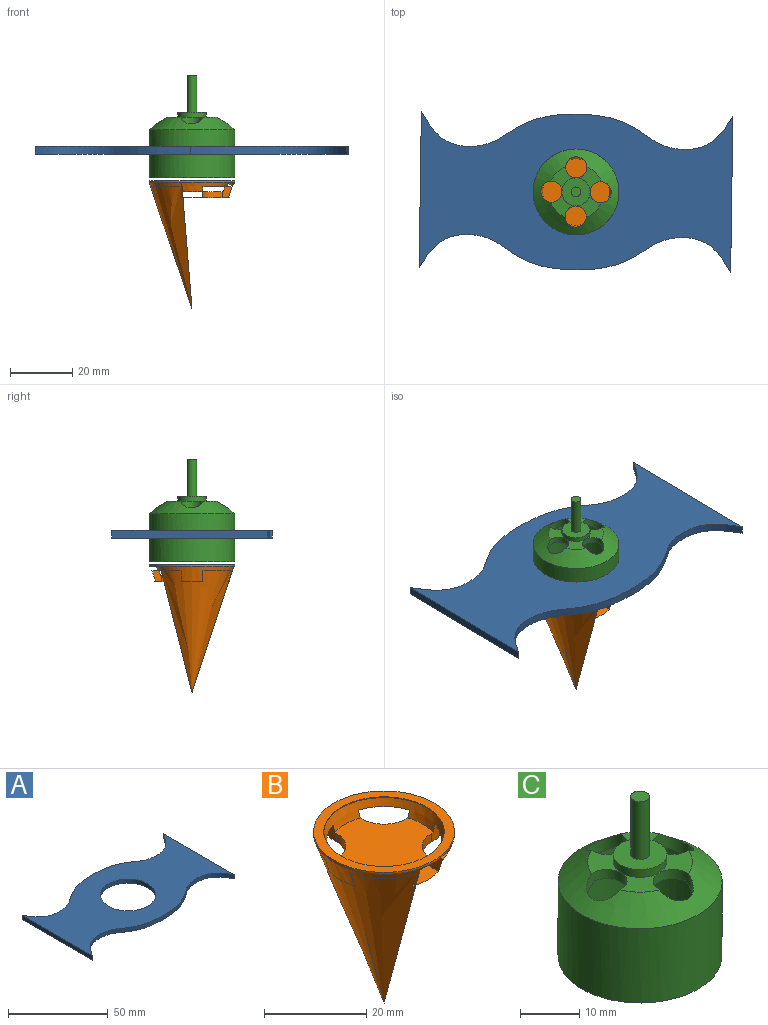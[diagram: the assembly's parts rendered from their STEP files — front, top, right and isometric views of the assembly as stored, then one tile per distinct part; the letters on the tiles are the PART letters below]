
ASSEMBLY  parts=3 mates=2
PART A: 9 faces, bbox 100x50x2.5 mm
  f0: plane 50x2.5mm, normal (-1,0,0), area 125mm2, adj f1,f6,f7,f8
  f1: extruded ~50x10.87mm, area 142.3mm2, adj f0,f2,f7,f8
  f2: extruded ~50x10.87mm, area 142.3mm2, adj f1,f3,f7,f8
  f3: plane 50x2.5mm, normal (1,0,0), area 125mm2, adj f2,f4,f7,f8
  f4: extruded ~50x10.87mm, area 142.3mm2, adj f3,f6,f7,f8
  f5: cylinder r=13.8mm len=27.6mm, axis (0,0,-1), area 216.8mm2, adj f7,f8
  f6: extruded ~50x10.87mm, area 142.3mm2, adj f0,f4,f7,f8
  f7: plane 100x50mm, normal (0,0,1), area 3287mm2, adj f0,f1,f2,f3,f4,f5,f6
  f8: plane 100x50mm, normal (0,0,-1), area 3287mm2, adj f0,f1,f2,f3,f4,f5,f6
PART B: 24 faces, bbox 27.6x27.6x5.5 mm
  f0: plane 24.2x24.2mm, normal (0,0,-1), area 317.6mm2, adj f1,f2,f3,f4,f5,f6,f7,f8
  f1: cylinder r=6.16mm len=6.16mm, axis (0,0,-1), area 19.3mm2, adj f0,f2,f14,f15
  f2: plane 3.62x3.22mm, normal (0,-1,0), area 8.1mm2, adj f0,f1,f3,f15,f16,f17
  f3: cone r=12.1mm half-angle=18.8deg, axis (0,0,1), area 196.3mm2, adj f0,f2,f4,f6,f7,f10,f11,f13
  f4: plane 3.62x3.22mm, normal (0,1,0), area 8.1mm2, adj f0,f3,f5,f15,f16,f18
  f5: cylinder r=6.16mm len=6.16mm, axis (0,0,-1), area 19.3mm2, adj f0,f4,f6,f15
  f6: plane 3.62x3.22mm, normal (-1,0,0), area 8.1mm2, adj f0,f3,f5,f15,f16,f18
  f7: plane 3.62x3.22mm, normal (1,0,0), area 8.1mm2, adj f0,f3,f8,f15,f16,f19
  f8: cylinder r=6.16mm len=6.16mm, axis (0,0,-1), area 19.3mm2, adj f0,f7,f9,f15
  f9: plane 3.62x3.22mm, normal (0,1,0), area 8.1mm2, adj f0,f8,f10,f15,f16,f19
  f10: cone r=12.1mm half-angle=18.8deg, axis (0,0,1), area 0.7mm2, adj f0,f3,f9,f21
  f11: plane 3.62x3.22mm, normal (0,-1,0), area 8.1mm2, adj f0,f3,f12,f15,f16,f20
  f12: cylinder r=6.16mm len=6.16mm, axis (0,0,-1), area 19.3mm2, adj f0,f11,f13,f15
  f13: plane 3.62x3.22mm, normal (1,0,0), area 8.1mm2, adj f0,f3,f12,f15,f16,f20
  f14: plane 3.62x3.22mm, normal (-1,0,0), area 8.1mm2, adj f0,f1,f3,f15,f16,f17
  f15: plane 21.34x21.34mm, normal (0,0,1), area 276.8mm2, adj f1,f2,f4,f5,f6,f7,f8,f9
  f16: cone r=10.21mm half-angle=18.8deg, axis (0,0,1), area 180.3mm2, adj f2,f4,f6,f7,f9,f11,f13,f14
  f17: plane 9.36x9.36mm, normal (0,0,-1), area 25.7mm2, adj f2,f3,f14,f16
  f18: plane 9.36x9.36mm, normal (0,0,-1), area 25.7mm2, adj f3,f4,f6,f16
  f19: plane 9.36x9.36mm, normal (0,0,-1), area 25.7mm2, adj f3,f7,f9,f16
  f20: plane 9.36x9.36mm, normal (0,0,-1), area 25.7mm2, adj f3,f11,f13,f16
  f21: cylinder r=13.8mm len=27.6mm, axis (0,0,1), area 43.4mm2, adj f10,f23
  f22: cylinder r=11.8mm len=23.6mm, axis (0,0,1), area 12.6mm2, adj f16,f23
  f23: plane 27.6x27.6mm, normal (0,0,1), area 160.8mm2, adj f21,f22
PART C: 20 faces, bbox 27.6x27.6x32.8 mm
  f0: plane 8.12x8.12mm, normal (0,0,1), area 22.2mm2, adj f6,f7,f18,f19
  f1: plane 8.12x8.12mm, normal (0,0,1), area 22.2mm2, adj f6,f7,f17,f18
  f2: plane 8.12x8.12mm, normal (0,0,1), area 22.2mm2, adj f6,f7,f16,f17
  f3: cylinder r=13.8mm len=27.6mm, axis (0,0,1), area 1326.6mm2, adj f4,f6
  f4: plane 27.6x27.6mm, normal (0,0,-1), area 153.4mm2, adj f3,f11
  f5: plane 8.12x8.12mm, normal (0,0,1), area 22.2mm2, adj f6,f7,f16,f19
  f6: cone r=8.8mm half-angle=51.3deg, axis (0,0,-1), area 385.2mm2, adj f0,f1,f2,f3,f5,f16,f17,f18
  f7: cylinder r=4.5mm len=9mm, axis (0,0,-1), area 45.2mm2, adj f0,f1,f2,f5,f8
  f8: plane 9x9mm, normal (0,0,1), area 55.9mm2, adj f7,f9
  f9: cylinder r=1.57mm len=11.9mm, axis (0,0,-1), area 117.4mm2, adj f8,f10
  f10: plane 3.14x3.14mm, normal (0,0,1), area 7.7mm2, adj f9
  f11: cylinder r=11.9mm len=23.8mm, axis (0,0,1), area 1075.7mm2, adj f4,f13
  f12: plane 14.81x14.81mm, normal (0,0,-1), area 114.2mm2, adj f13,f14,f16,f17,f18,f19
  f13: cone r=7.61mm half-angle=51.3deg, axis (0,0,-1), area 210.3mm2, adj f11,f12,f16,f17,f18,f19
  f14: cylinder r=2.6mm len=5.2mm, axis (0,0,-1), area 26.1mm2, adj f12,f15
  f15: plane 5.2x5.2mm, normal (0,0,-1), area 21.2mm2, adj f14
  f16: cylinder r=3.4mm len=6.8mm, axis (0,0,1), area 46.4mm2, adj f2,f5,f6,f12,f13
  f17: cylinder r=3.4mm len=6.8mm, axis (0,0,1), area 46.4mm2, adj f1,f2,f6,f12,f13
  f18: cylinder r=3.4mm len=6.8mm, axis (0,0,1), area 46.4mm2, adj f0,f1,f6,f12,f13
  f19: cylinder r=3.4mm len=6.8mm, axis (0,0,1), area 46.4mm2, adj f0,f5,f6,f12,f13
PLACE A rot(axis=(0,0,-1),0.8deg) t=(1.38,-3.22,23.93)mm
PLACE B t=(1.38,-3.22,35.13)mm fixed
PLACE C rot(axis=(0,0,-1),0.8deg) t=(1.38,-3.22,35.73)mm
MATE parallel A.f5 <-> C.f3  axis (0,0,1) through (1.38,-3.22,26.43)mm
MATE revolute C.f3 <-> B.f3  axis (0,0,1) through (1.38,-3.22,16.43)mm
